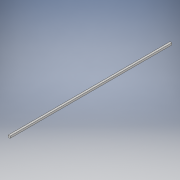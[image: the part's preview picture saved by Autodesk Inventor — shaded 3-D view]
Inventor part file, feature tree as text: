
AUTODESK INVENTOR PART (.ipt)
format: ipt  version: 2017 (Build 210142000, 142)  size: 92,160 bytes
history: native  units: in
note: dims shown in document units (in); Inventor stores cm internally (conversion verified against a paired STEP export)
features: extrude x1, sketch x1
ambient origin geometry x8: Origin, YZ Plane, XZ Plane, XY Plane, X Axis, Y Axis, Z Axis, Center Point
bodies: Solid1 (feature_tree)
feature tree (2):
  extrude  "Extrusion1"  Depth=0.125in
  sketch  "Sketch1"  dims[d0=0.125in d1=0.125in d2=10.5in d3=0.0in]
